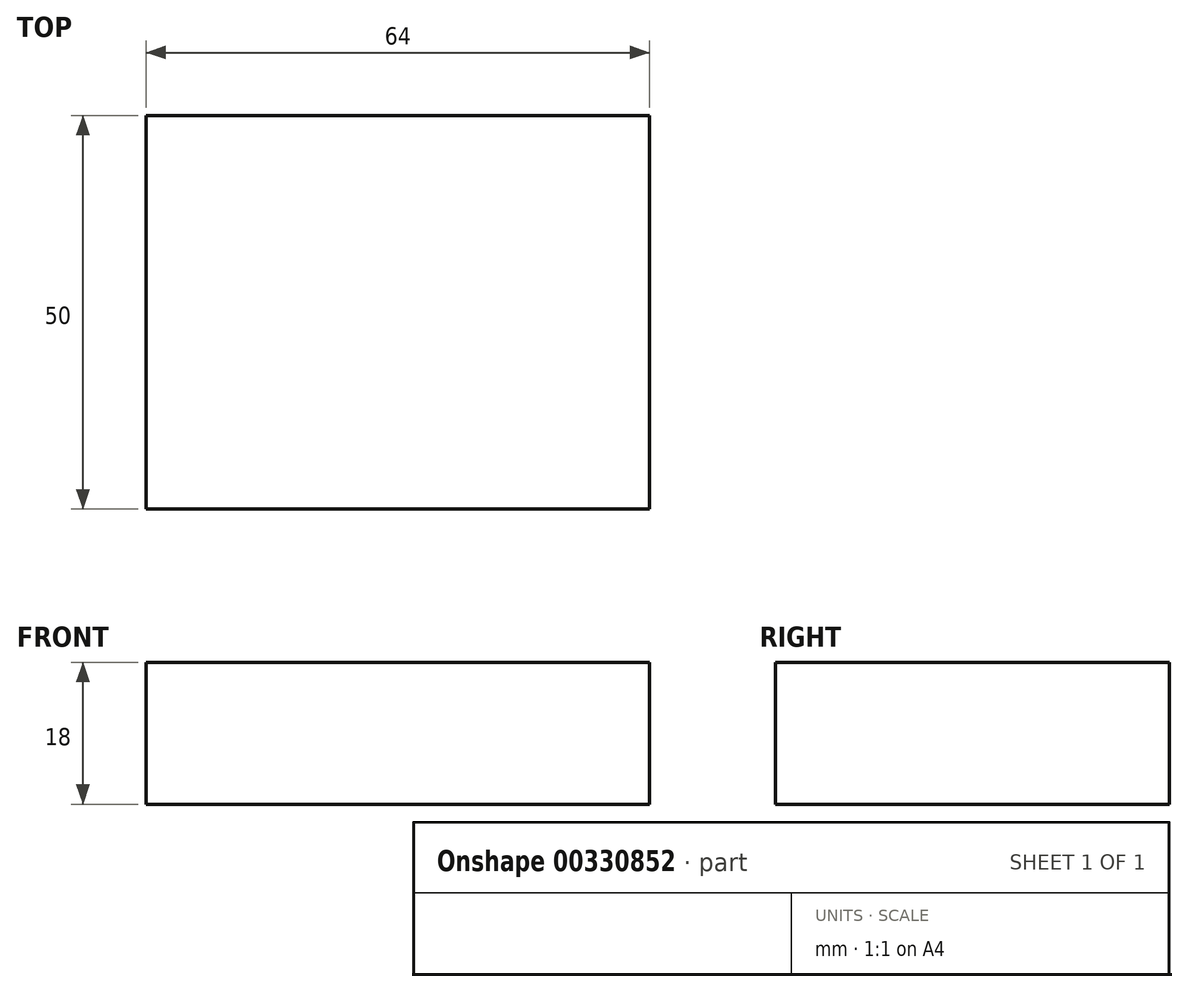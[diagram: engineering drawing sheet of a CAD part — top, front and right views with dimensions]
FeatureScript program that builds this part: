
annotation { "Feature Type Name" : "Feature", "Feature Type Description" : "" }
export const myFeature = defineFeature(function(context is Context, id is Id, definition is map)
    precondition{}
    {
        {
            var Q0;
            Q0=qCreatedBy(makeId("Top.planeOp"),FACE);
            var sketch = newSketch(context, id + "F0", { "sketchPlane" : qUnion([Q0])});
            skLineSegment(sketch, "E0.bottom", {"start": v(-18.92, 21.75) * mm, "end": v(45.08, 21.75) * mm});
            skLineSegment(sketch, "E0.top", {"start": v(-18.92, -28.25) * mm, "end": v(45.08, -28.25) * mm});
            skLineSegment(sketch, "E0.left", {"start": v(-18.92, 21.75) * mm, "end": v(-18.92, -28.25) * mm});
            skLineSegment(sketch, "E0.right", {"start": v(45.08, 21.75) * mm, "end": v(45.08, -28.25) * mm});
            skSolve(sketch);
        }
        {
            var Q0;
            Q0=makeQuery(id+"F0.imprint","IMPRINT",FACE,{"disambiguationData":[TD([[makeQuery(id+"F0.imprint","IMPRINT",EDGE,{"derivedFrom":sQuery(id+"F0.wireOp",EDGE,"E0.bottom")}),-1.0]])]});
            extrude(context, id + "F1", {"entities" : qUnion([Q0]), "depth" : 18 * mm});
        }
    });
